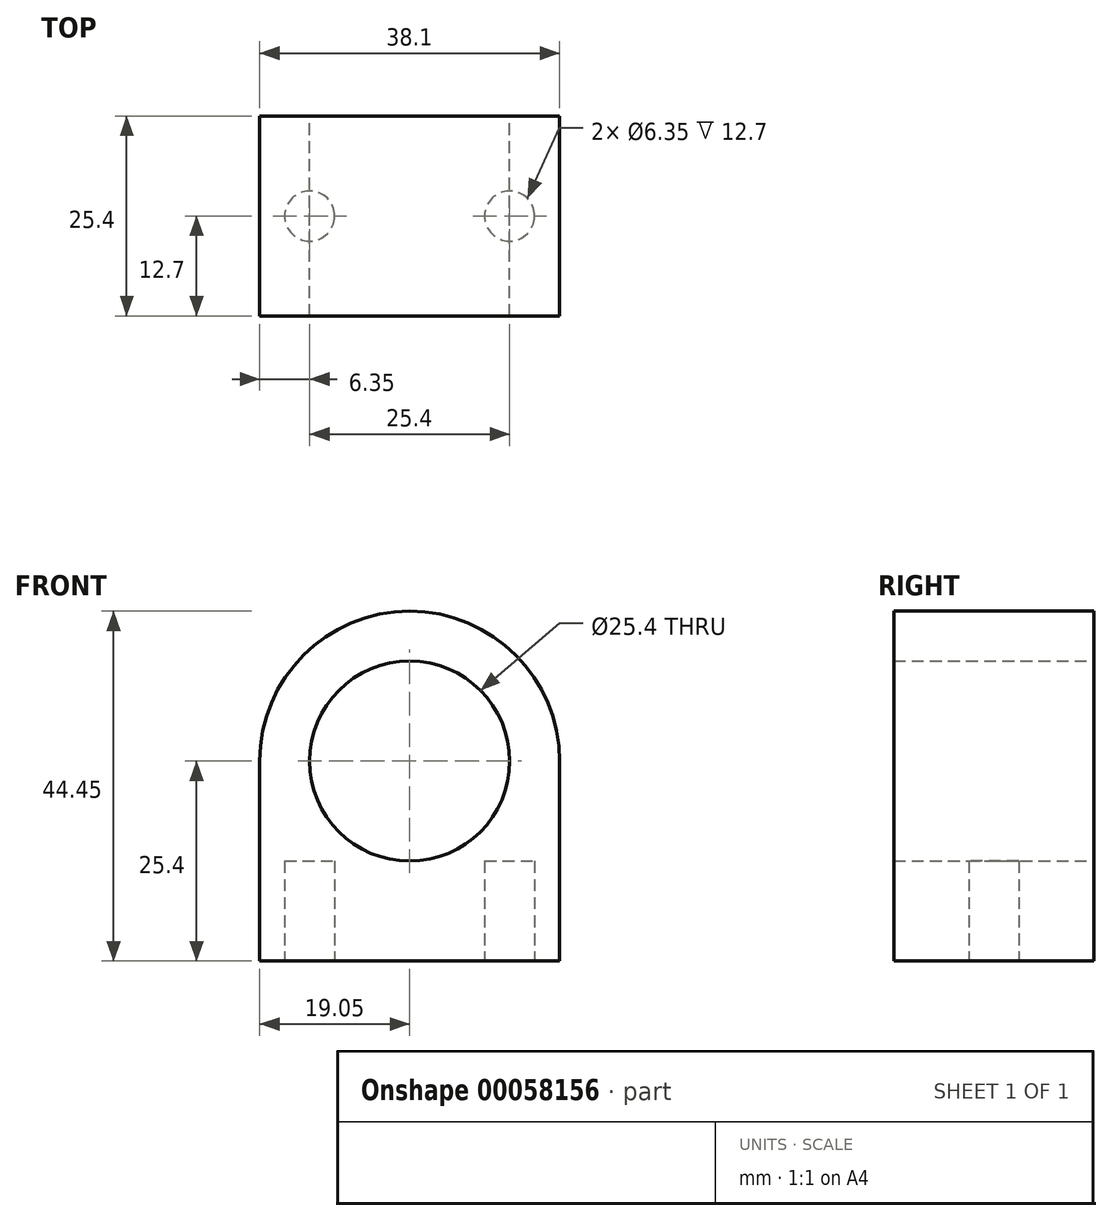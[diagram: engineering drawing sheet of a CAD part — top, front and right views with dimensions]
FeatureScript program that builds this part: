
annotation { "Feature Type Name" : "Feature", "Feature Type Description" : "" }
export const myFeature = defineFeature(function(context is Context, id is Id, definition is map)
    precondition{}
    {
        {
            var Q0;
            Q0=qCreatedBy(makeId("Front.planeOp"),FACE);
            var sketch = newSketch(context, id + "F0", { "sketchPlane" : qUnion([Q0])});
            skCircle(sketch, "E0", {"center": v(0, 0) * mm, "radius": 12.7 * mm});
            skArc(sketch, "E1", {"start": v(19.05, 0) * mm, "mid": v(0, 19.05) * mm, "end": v(-19.05, 0) * mm});
            skLineSegment(sketch, "E2", {"start": v(-19.05, 0) * mm, "end": v(-19.05, -25.4) * mm});
            skLineSegment(sketch, "E3", {"start": v(-19.05, -25.4) * mm, "end": v(19.05, -25.4) * mm});
            skLineSegment(sketch, "E4", {"start": v(19.05, -25.4) * mm, "end": v(19.05, 0) * mm});
            skSolve(sketch);
        }
        {
            var Q0;
            Q0=makeQuery(id+"F0.imprint","IMPRINT",FACE,{"disambiguationData":[TD([[makeQuery(id+"F0.imprint","IMPRINT",EDGE,{"derivedFrom":sQuery(id+"F0.wireOp",EDGE,"E0")}),-1.0]])]});
            extrude(context, id + "F1", {"entities" : qUnion([Q0]), "depth" : 25.4 * mm});
        }
        {
            var Q0;
            Q0=makeQuery(id+"F1.opExtrude","SWEPT_FACE",FACE,{"disambiguationData":[OSD([sQuery(id+"F0.wireOp",EDGE,"E3")])]});
            var sketch = newSketch(context, id + "F2", { "sketchPlane" : qUnion([Q0])});
            skCircle(sketch, "E5", {"center": v(-12.7, 12.7) * mm, "radius": 3.17 * mm});
            skCircle(sketch, "E6", {"center": v(12.7, 12.7) * mm, "radius": 3.18 * mm});
            skSolve(sketch);
        }
        {
            var Q0;
            Q0=makeQuery(id+"F2.imprint","IMPRINT",FACE,{"disambiguationData":[TD([[makeQuery(id+"F2.imprint","IMPRINT",EDGE,{"derivedFrom":sQuery(id+"F2.wireOp",EDGE,"E6")}),1.0]])]});
            var Q1;
            Q1=makeQuery(id+"F2.imprint","IMPRINT",FACE,{"disambiguationData":[TD([[makeQuery(id+"F2.imprint","IMPRINT",EDGE,{"derivedFrom":sQuery(id+"F2.wireOp",EDGE,"E5")}),1.0]])]});
            extrude(context, id + "F3", {"entities" : qUnion([Q0, Q1]), "operationType" : NewBodyOperationType.REMOVE, "oppositeDirection" : true, "depth" : 12.7 * mm});
        }
    });
